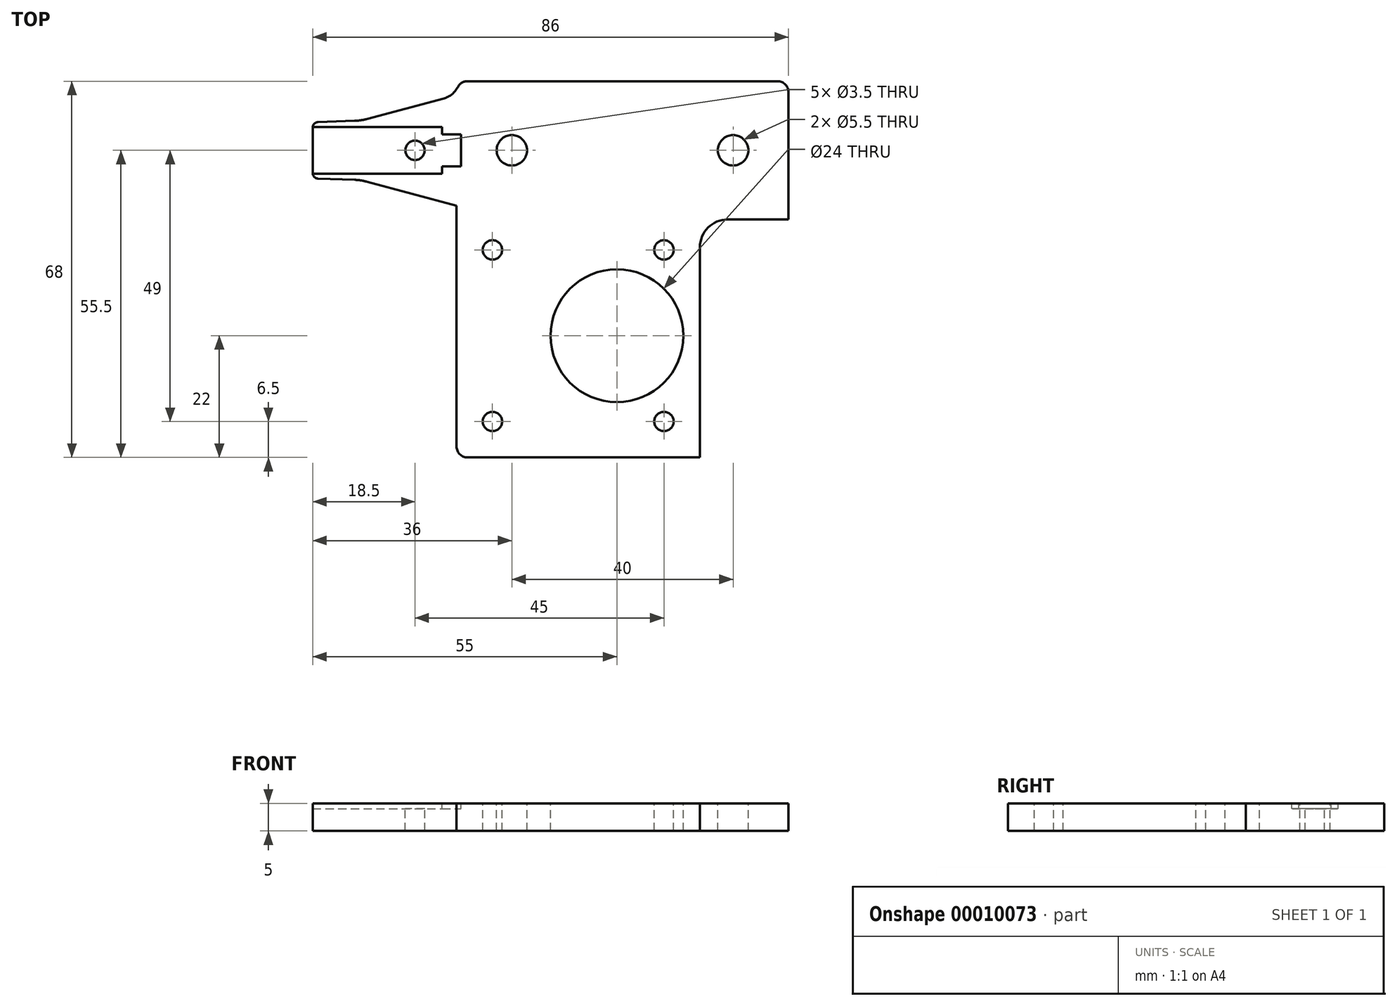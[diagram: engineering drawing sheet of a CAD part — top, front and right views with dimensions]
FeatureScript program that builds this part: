
annotation { "Feature Type Name" : "Feature", "Feature Type Description" : "" }
export const myFeature = defineFeature(function(context is Context, id is Id, definition is map)
    precondition{}
    {
        {
            var Q0;
            Q0=qCreatedBy(makeId("Top.planeOp"),FACE);
            var sketch = newSketch(context, id + "F0", { "sketchPlane" : qUnion([Q0])});
            skLineSegment(sketch, "E0.rect.bottom", {"start": v(-30, 34) * mm, "end": v(30, 34) * mm});
            skLineSegment(sketch, "E0.rect.top", {"start": v(-30, -34) * mm, "end": v(30, -34) * mm});
            skLineSegment(sketch, "E0.rect.left", {"start": v(-30, 34) * mm, "end": v(-30, -34) * mm});
            skLineSegment(sketch, "E0.rect.right", {"start": v(30, 34) * mm, "end": v(30, -34) * mm});
            skPoint(sketch, "E0.rect.middle", {"position": v(0, 0) * mm});
            skSolve(sketch);
        }
        {
            var Q0;
            Q0=makeQuery(id+"F0.imprint","IMPRINT",FACE,{"disambiguationData":[TD([[makeQuery(id+"F0.imprint","IMPRINT",EDGE,{"derivedFrom":sQuery(id+"F0.wireOp",EDGE,"E0.rect.bottom")}),-1.0]])]});
            extrude(context, id + "F1", {"entities" : qUnion([Q0]), "depth" : 5 * mm});
        }
        {
            var Q0;
            Q0=makeQuery(id+"F1.opExtrude","CAP_FACE",FACE,{"disambiguationData":[OSD([sQuery(id+"F0.wireOp",EDGE,"E0.rect.bottom"),sQuery(id+"F0.wireOp",EDGE,"E0.rect.top"),sQuery(id+"F0.wireOp",EDGE,"E0.rect.left"),sQuery(id+"F0.wireOp",EDGE,"E0.rect.right")])],"isStart":false});
            var sketch = newSketch(context, id + "F2", { "sketchPlane" : qUnion([Q0])});
            skLineSegment(sketch, "E1.bottom", {"start": v(30, -34) * mm, "end": v(14, -34) * mm});
            skLineSegment(sketch, "E1.top", {"start": v(30, 9) * mm, "end": v(14, 9) * mm});
            skLineSegment(sketch, "E1.left", {"start": v(30, -34) * mm, "end": v(30, 9) * mm});
            skLineSegment(sketch, "E1.right", {"start": v(14, -34) * mm, "end": v(14, 9) * mm});
            skSolve(sketch);
        }
        {
            var Q0;
            Q0=makeQuery(id+"F2.imprint","IMPRINT",FACE,{"disambiguationData":[TD([[makeQuery(id+"F2.imprint","IMPRINT",EDGE,{"derivedFrom":sQuery(id+"F2.wireOp",EDGE,"E1.bottom")}),1.0]])]});
            extrude(context, id + "F3", {"entities" : qUnion([Q0]), "operationType" : NewBodyOperationType.REMOVE, "endBound" : BoundingType.THROUGH_ALL, "oppositeDirection" : true, "depth" : 25 * mm});
        }
        {
            var Q0;
            Q0=makeQuery(id+"F1.opExtrude","CAP_FACE",FACE,{"disambiguationData":[OSD([sQuery(id+"F0.wireOp",EDGE,"E0.rect.bottom"),sQuery(id+"F0.wireOp",EDGE,"E0.rect.top"),sQuery(id+"F0.wireOp",EDGE,"E0.rect.left"),sQuery(id+"F0.wireOp",EDGE,"E0.rect.right")])],"isStart":false});
            var sketch = newSketch(context, id + "F4", { "sketchPlane" : qUnion([Q0])});
            skCircle(sketch, "E2", {"center": v(-1, -12) * mm, "radius": 12 * mm});
            skCircle(sketch, "E3", {"center": v(-23.5, -27.5) * mm, "radius": 1.75 * mm});
            skCircle(sketch, "E4", {"center": v(7.5, -27.5) * mm, "radius": 1.75 * mm});
            skCircle(sketch, "E5", {"center": v(7.5, 3.5) * mm, "radius": 1.75 * mm});
            skCircle(sketch, "E6", {"center": v(-23.5, 3.5) * mm, "radius": 1.75 * mm});
            skLineSegment(sketch, "E7", {"start": v(11, -34) * mm, "end": v(11, 9) * mm, "construction": true});
            skSolve(sketch);
        }
        {
            var Q0;
            Q0=qSketchRegion(id+"F4",true);
            extrude(context, id + "F5", {"entities" : qUnion([Q0]), "operationType" : NewBodyOperationType.REMOVE, "endBound" : BoundingType.THROUGH_ALL, "oppositeDirection" : true, "depth" : 25 * mm});
        }
        {
            var Q0;
            Q0=makeQuery(id+"F1.opExtrude","CAP_FACE",FACE,{"disambiguationData":[OSD([sQuery(id+"F0.wireOp",EDGE,"E0.rect.bottom"),sQuery(id+"F0.wireOp",EDGE,"E0.rect.top"),sQuery(id+"F0.wireOp",EDGE,"E0.rect.left"),sQuery(id+"F0.wireOp",EDGE,"E0.rect.right")])],"isStart":false});
            var sketch = newSketch(context, id + "F6", { "sketchPlane" : qUnion([Q0])});
            skCircle(sketch, "E8", {"center": v(-20, 21.5) * mm, "radius": 2.75 * mm});
            skCircle(sketch, "E9", {"center": v(20, 21.5) * mm, "radius": 2.75 * mm});
            skSolve(sketch);
        }
        {
            var Q0;
            Q0=qSketchRegion(id+"F6",true);
            extrude(context, id + "F7", {"entities" : qUnion([Q0]), "operationType" : NewBodyOperationType.REMOVE, "endBound" : BoundingType.THROUGH_ALL, "oppositeDirection" : true, "depth" : 25 * mm});
        }
        {
            var Q0;
            Q0=makeQuery(id+"F3.boolean.opBoolean","COPY",EDGE,{"derivedFrom":makeQuery(id+"F3.opExtrude","SWEPT_EDGE",EDGE,{"disambiguationData":[OSD([sQuery(id+"F2.wireOp",EDGE,"E1.top"),sQuery(id+"F2.wireOp",EDGE,"E1.right")])]})});
            fillet(context, id + "F8", {"entities" : qUnion([Q0]), "radius" : 5 * mm, "tangentPropagation" : true, "allowEdgeOverflow" : false});
        }
        {
            var Q0;
            Q0=makeQuery(id+"F1.opExtrude","SWEPT_EDGE",EDGE,{"disambiguationData":[OSD([sQuery(id+"F0.wireOp",EDGE,"E0.rect.top"),sQuery(id+"F0.wireOp",EDGE,"E0.rect.left")])]});
            var Q1;
            Q1=makeQuery(id+"F1.opExtrude","SWEPT_EDGE",EDGE,{"disambiguationData":[OSD([sQuery(id+"F0.wireOp",EDGE,"E0.rect.bottom"),sQuery(id+"F0.wireOp",EDGE,"E0.rect.left")])]});
            var Q2;
            Q2=makeQuery(id+"F3.boolean.opBoolean","COPY",EDGE,{"derivedFrom":makeQuery(id+"F3.opExtrude","SWEPT_EDGE",EDGE,{"disambiguationData":[OSD([sQuery(id+"F0.wireOp",EDGE,"E0.rect.right"),sQuery(id+"F2.wireOp",EDGE,"E1.top"),sQuery(id+"F2.wireOp",EDGE,"E1.left")])]})});
            var Q3;
            Q3=makeQuery(id+"F1.opExtrude","SWEPT_EDGE",EDGE,{"disambiguationData":[OSD([sQuery(id+"F0.wireOp",EDGE,"E0.rect.bottom"),sQuery(id+"F0.wireOp",EDGE,"E0.rect.right")])]});
            var Q4;
            Q4=makeQuery(id+"F3.boolean.opBoolean","COPY",EDGE,{"derivedFrom":makeQuery(id+"F3.opExtrude","SWEPT_EDGE",EDGE,{"disambiguationData":[OSD([sQuery(id+"F0.wireOp",EDGE,"E0.rect.top"),sQuery(id+"F2.wireOp",EDGE,"E1.bottom"),sQuery(id+"F2.wireOp",EDGE,"E1.right")])]})});
            fillet(context, id + "F9", {"entities" : qUnion([Q0, Q1, Q2, Q3, Q4]), "radius" : 2 * mm, "tangentPropagation" : true, "allowEdgeOverflow" : false});
        }
        {
            var Q0;
            Q0=makeQuery(id+"F1.opExtrude","CAP_FACE",FACE,{"disambiguationData":[OSD([sQuery(id+"F0.wireOp",EDGE,"E0.rect.bottom"),sQuery(id+"F0.wireOp",EDGE,"E0.rect.top"),sQuery(id+"F0.wireOp",EDGE,"E0.rect.left"),sQuery(id+"F0.wireOp",EDGE,"E0.rect.right")])],"isStart":false});
            var sketch = newSketch(context, id + "F10", { "sketchPlane" : qUnion([Q0])});
            skLineSegment(sketch, "E10.right", {"start": v(-56, 16.43) * mm, "end": v(-56, 26.58) * mm});
            skLineSegment(sketch, "E11", {"start": v(-56, 16.43) * mm, "end": v(-47.26, 16.12) * mm});
            skLineSegment(sketch, "E12", {"start": v(-47.26, 16.12) * mm, "end": v(-30, 11.5) * mm});
            skLineSegment(sketch, "E13", {"start": v(-56, 26.58) * mm, "end": v(-47.26, 26.88) * mm});
            skLineSegment(sketch, "E14", {"start": v(-47.26, 26.88) * mm, "end": v(-30, 31.5) * mm});
            skLineSegment(sketch, "E15", {"start": v(-30, 31.5) * mm, "end": v(-30, 11.5) * mm});
            skLineSegment(sketch, "E16", {"start": v(-56, 21.5) * mm, "end": v(-30, 21.5) * mm, "construction": true});
            skSolve(sketch);
        }
        {
            var Q0;
            Q0=qSketchRegion(id+"F10",true);
            extrude(context, id + "F11", {"entities" : qUnion([Q0]), "oppositeDirection" : true, "depth" : 5 * mm});
        }
        {
            var Q0;
            Q0=makeQuery(id+"F11.opExtrude","SWEPT_BODY",BODY,{"disambiguationData":[OSD([sQuery(id+"F10.wireOp",EDGE,"E10.right"),sQuery(id+"F10.wireOp",EDGE,"E11"),sQuery(id+"F10.wireOp",EDGE,"E12"),sQuery(id+"F10.wireOp",EDGE,"E13"),sQuery(id+"F10.wireOp",EDGE,"E14"),sQuery(id+"F10.wireOp",EDGE,"E15")])]});
            var Q1;
            Q1=makeQuery(id+"F1.opExtrude","SWEPT_BODY",BODY,{"disambiguationData":[OSD([sQuery(id+"F0.wireOp",EDGE,"E0.rect.bottom"),sQuery(id+"F0.wireOp",EDGE,"E0.rect.top"),sQuery(id+"F0.wireOp",EDGE,"E0.rect.left"),sQuery(id+"F0.wireOp",EDGE,"E0.rect.right")])]});
            booleanBodies(context, id + "F12", {"operationType" : BooleanOperationType.UNION, "tools" : qUnion([Q0, Q1])});
        }
        {
            var Q0;
            Q0=makeQuery(id+"F11.opExtrude","SWEPT_EDGE",EDGE,{"disambiguationData":[OSD([sQuery(id+"F0.wireOp",EDGE,"E0.rect.left"),sQuery(id+"F10.wireOp",EDGE,"E12"),sQuery(id+"F10.wireOp",EDGE,"E15")])]});
            var Q1;
            Q1=makeQuery(id+"F11.opExtrude","SWEPT_EDGE",EDGE,{"disambiguationData":[OSD([sQuery(id+"F0.wireOp",EDGE,"E0.rect.left"),sQuery(id+"F10.wireOp",EDGE,"E14"),sQuery(id+"F10.wireOp",EDGE,"E15")])]});
            fillet(context, id + "F13", {"entities" : qUnion([Q0, Q1]), "radius" : 4 * mm, "tangentPropagation" : true, "allowEdgeOverflow" : false});
        }
        {
            var Q0;
            Q0=makeQuery(id+"F11.opExtrude","SWEPT_EDGE",EDGE,{"disambiguationData":[OSD([sQuery(id+"F10.wireOp",EDGE,"E11"),sQuery(id+"F10.wireOp",EDGE,"E12")])]});
            var Q1;
            Q1=makeQuery(id+"F11.opExtrude","SWEPT_EDGE",EDGE,{"disambiguationData":[OSD([sQuery(id+"F10.wireOp",EDGE,"E13"),sQuery(id+"F10.wireOp",EDGE,"E14")])]});
            fillet(context, id + "F14", {"entities" : qUnion([Q0, Q1]), "radius" : 10 * mm, "tangentPropagation" : true, "allowEdgeOverflow" : false});
        }
        {
            var Q0;
            Q0=makeQuery(id+"F0olbTQd7KgvNAM_2.boolean.opBoolean","MERGE",EDGE,{"derivedFrom":[makeQuery(id+"F11.opExtrude","SWEPT_EDGE",EDGE,{"disambiguationData":[OSD([sQuery(id+"F10.wireOp",EDGE,"E10.right"),sQuery(id+"F10.wireOp",EDGE,"E13")])]}),makeQuery(id+"F0olbTQd7KgvNAM_2.opExtrude","SWEPT_EDGE",EDGE,{"disambiguationData":[OSD([sQuery(id+"FT5JVraEqX45OWP_2.wireOp",EDGE,"cfad28e6-80b3-47dd-a36c-e803d7988366"),sQuery(id+"FT5JVraEqX45OWP_2.wireOp",EDGE,"1ae78de4-b477-4031-bc35-6b7f3ec27295")])]})]});
            var Q1;
            Q1=makeQuery(id+"F0olbTQd7KgvNAM_2.boolean.opBoolean","MERGE",EDGE,{"derivedFrom":[makeQuery(id+"F11.opExtrude","SWEPT_EDGE",EDGE,{"disambiguationData":[OSD([sQuery(id+"F10.wireOp",EDGE,"E10.right"),sQuery(id+"F10.wireOp",EDGE,"E11")])]}),makeQuery(id+"F0olbTQd7KgvNAM_2.opExtrude","SWEPT_EDGE",EDGE,{"disambiguationData":[OSD([sQuery(id+"FT5JVraEqX45OWP_2.wireOp",EDGE,"cfe2abfe-dc3e-4df3-afd2-d37dfddbcdff"),sQuery(id+"FT5JVraEqX45OWP_2.wireOp",EDGE,"aaf28f13-601e-4395-9753-1f5e5a479b1d")])]})]});
            fillet(context, id + "F15", {"entities" : qUnion([Q0, Q1]), "radius" : 1.03 * mm, "tangentPropagation" : true, "allowEdgeOverflow" : false});
        }
        {
            var Q0;
            Q0=makeQuery(id+"F12.opBoolean","MERGE",FACE,{"derivedFrom":[makeQuery(id+"F1.opExtrude","CAP_FACE",FACE,{"disambiguationData":[OSD([sQuery(id+"F0.wireOp",EDGE,"E0.rect.bottom"),sQuery(id+"F0.wireOp",EDGE,"E0.rect.top"),sQuery(id+"F0.wireOp",EDGE,"E0.rect.left"),sQuery(id+"F0.wireOp",EDGE,"E0.rect.right")])],"isStart":false}),makeQuery(id+"F11.opExtrude","CAP_FACE",FACE,{"disambiguationData":[OSD([sQuery(id+"F10.wireOp",EDGE,"E10.right"),sQuery(id+"F10.wireOp",EDGE,"E11"),sQuery(id+"F10.wireOp",EDGE,"E12"),sQuery(id+"F10.wireOp",EDGE,"E13"),sQuery(id+"F10.wireOp",EDGE,"E14"),sQuery(id+"F10.wireOp",EDGE,"E15")])],"isStart":true})]});
            var sketch = newSketch(context, id + "F16", { "sketchPlane" : qUnion([Q0])});
            skCircle(sketch, "E17", {"center": v(-37.5, 21.5) * mm, "radius": 1.75 * mm});
            skSolve(sketch);
        }
        {
            var Q0;
            Q0=makeQuery(id+"F16.imprint","IMPRINT",FACE,{"disambiguationData":[TD([[makeQuery(id+"F16.imprint","IMPRINT",EDGE,{"derivedFrom":sQuery(id+"F16.wireOp",EDGE,"E17")}),1.0]])]});
            extrude(context, id + "F17", {"entities" : qUnion([Q0]), "operationType" : NewBodyOperationType.REMOVE, "endBound" : BoundingType.THROUGH_ALL, "oppositeDirection" : true, "depth" : 25 * mm});
        }
        {
            var Q0;
            Q0=makeQuery(id+"F12.opBoolean","MERGE",FACE,{"derivedFrom":[makeQuery(id+"F1.opExtrude","CAP_FACE",FACE,{"disambiguationData":[OSD([sQuery(id+"F0.wireOp",EDGE,"E0.rect.bottom"),sQuery(id+"F0.wireOp",EDGE,"E0.rect.top"),sQuery(id+"F0.wireOp",EDGE,"E0.rect.left"),sQuery(id+"F0.wireOp",EDGE,"E0.rect.right")])],"isStart":false}),makeQuery(id+"F11.opExtrude","CAP_FACE",FACE,{"disambiguationData":[OSD([sQuery(id+"F10.wireOp",EDGE,"E10.right"),sQuery(id+"F10.wireOp",EDGE,"E11"),sQuery(id+"F10.wireOp",EDGE,"E12"),sQuery(id+"F10.wireOp",EDGE,"E13"),sQuery(id+"F10.wireOp",EDGE,"E14"),sQuery(id+"F10.wireOp",EDGE,"E15")])],"isStart":true})]});
            var sketch = newSketch(context, id + "F18", { "sketchPlane" : qUnion([Q0])});
            skLineSegment(sketch, "E18.top", {"start": v(-56, 17.3) * mm, "end": v(-32.6, 17.3) * mm});
            skLineSegment(sketch, "E18.left", {"start": v(-56, 25.7) * mm, "end": v(-56, 17.3) * mm});
            skLineSegment(sketch, "E18.right", {"start": v(-32.6, 25.7) * mm, "end": v(-32.6, 24.4) * mm});
            skLineSegment(sketch, "E19.bottom", {"start": v(-32.6, 24.4) * mm, "end": v(-29.2, 24.4) * mm});
            skLineSegment(sketch, "E19.top", {"start": v(-32.6, 18.6) * mm, "end": v(-29.2, 18.6) * mm});
            skLineSegment(sketch, "E19.right", {"start": v(-29.2, 24.4) * mm, "end": v(-29.2, 18.6) * mm});
            skLineSegment(sketch, "E20.trimOffspring", {"start": v(-32.6, 18.6) * mm, "end": v(-32.6, 17.3) * mm});
            skLineSegment(sketch, "E21", {"start": v(-29.2, 21.5) * mm, "end": v(-56, 21.5) * mm, "construction": true});
            skLineSegment(sketch, "E22", {"start": v(-56, 25.7) * mm, "end": v(-32.6, 25.7) * mm});
            skSolve(sketch);
        }
        {
            var Q0;
            {var subQ1=sQuery(id+"F18.wireOp",EDGE,"E18.left");Q0=makeQuery(id+"F18.imprint","IMPRINT",FACE,{"disambiguationData":[TD([[makeQuery(id+"F18.imprint","IMPRINT",EDGE,{"derivedFrom":subQ1}),-1.0]])]});}
            extrude(context, id + "F19", {"entities" : qUnion([Q0]), "operationType" : NewBodyOperationType.REMOVE, "oppositeDirection" : true, "depth" : 1 * mm});
        }
    });
